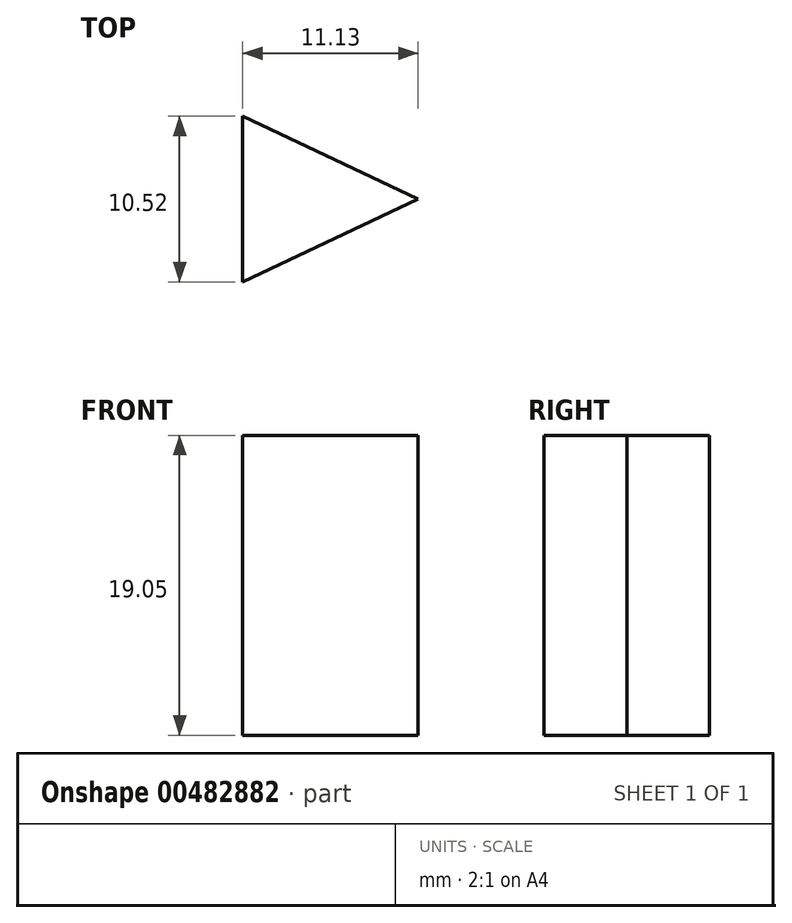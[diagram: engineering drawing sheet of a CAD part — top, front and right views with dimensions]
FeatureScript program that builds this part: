
annotation { "Feature Type Name" : "Feature", "Feature Type Description" : "" }
export const myFeature = defineFeature(function(context is Context, id is Id, definition is map)
    precondition{}
    {
        {
            var Q0;
            Q0=qCreatedBy(makeId("Top.planeOp"),FACE);
            var sketch = newSketch(context, id + "F0", { "sketchPlane" : qUnion([Q0])});
            skLineSegment(sketch, "E0", {"start": v(0, 0) * mm, "end": v(106.78, 0) * mm});
            skLineSegment(sketch, "E1", {"start": v(-106.78, 0) * mm, "end": v(-95.65, 0) * mm});
            skLineSegment(sketch, "E2", {"start": v(-95.65, 0) * mm, "end": v(-106.78, 5.26) * mm});
            skLineSegment(sketch, "E3", {"start": v(-106.78, 5.26) * mm, "end": v(-106.78, 0) * mm});
            skLineSegment(sketch, "E4", {"start": v(-95.65, 0) * mm, "end": v(-106.78, -5.26) * mm});
            skLineSegment(sketch, "E5", {"start": v(-106.78, -5.26) * mm, "end": v(-106.78, 0) * mm});
            skSolve(sketch);
        }
        {
            var Q0;
            Q0=makeQuery(id+"F0.imprint","IMPRINT",FACE,{"disambiguationData":[TD([[makeQuery(id+"F0.imprint","IMPRINT",EDGE,{"derivedFrom":sQuery(id+"F0.wireOp",EDGE,"E1")}),-1.0]])]});
            var Q1;
            Q1=makeQuery(id+"F0.imprint","IMPRINT",FACE,{"disambiguationData":[TD([[makeQuery(id+"F0.imprint","IMPRINT",EDGE,{"derivedFrom":sQuery(id+"F0.wireOp",EDGE,"E1")}),1.0]])]});
            extrude(context, id + "F1", {"entities" : qUnion([Q0, Q1]), "depth" : 19.05 * mm, "offsetDistance" : 25.4 * mm});
        }
    });
